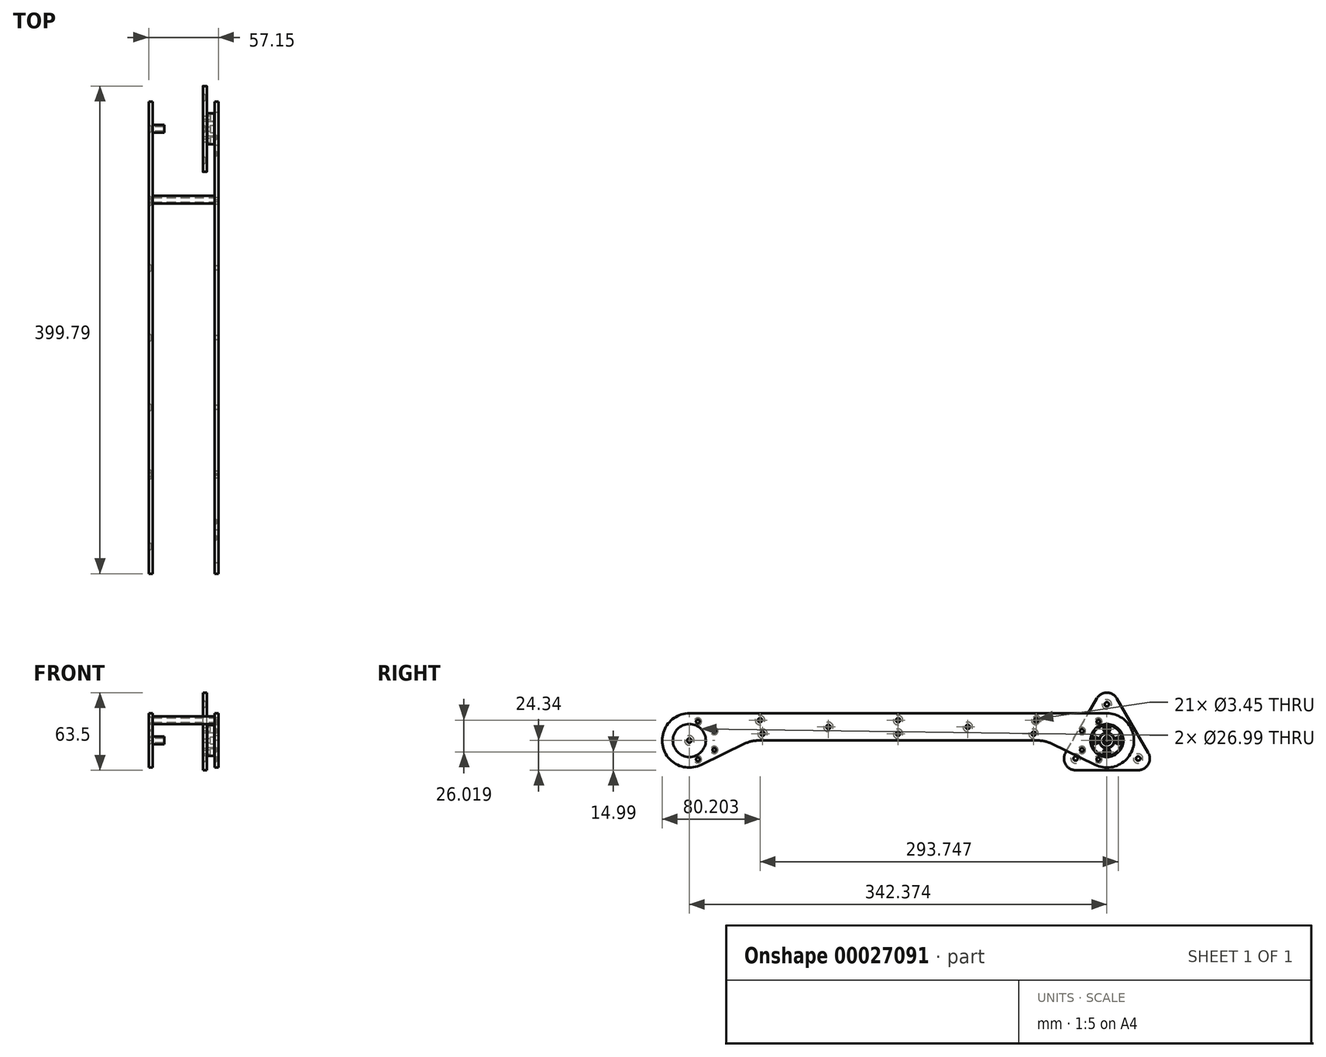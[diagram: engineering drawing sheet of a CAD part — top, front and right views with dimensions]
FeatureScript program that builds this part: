
annotation { "Feature Type Name" : "Feature", "Feature Type Description" : "" }
export const myFeature = defineFeature(function(context is Context, id is Id, definition is map)
    precondition{}
    {
        {
            var Q0;
            Q0=qCreatedBy(makeId("Right.planeOp"),FACE);
            var sketch = newSketch(context, id + "F0", { "sketchPlane" : qUnion([Q0])});
            skCircle(sketch, "E0.cCircle", {"center": v(0, 0) * mm, "radius": 29.63 * mm, "construction": true});
            skLineSegment(sketch, "E0.0", {"start": v(25.66, -14.82) * mm, "end": v(-25.66, -14.82) * mm, "construction": true});
            skLineSegment(sketch, "E0.1", {"start": v(-25.66, -14.82) * mm, "end": v(0, 29.63) * mm, "construction": true});
            skLineSegment(sketch, "E0.2", {"start": v(0, 29.63) * mm, "end": v(25.66, -14.82) * mm, "construction": true});
            skCircle(sketch, "E1", {"center": v(25.66, -14.82) * mm, "radius": 25.4 * mm});
            skCircle(sketch, "E2", {"center": v(-25.66, -14.82) * mm, "radius": 25.4 * mm});
            skCircle(sketch, "E3", {"center": v(0, 29.63) * mm, "radius": 25.4 * mm});
            skCircle(sketch, "E4", {"center": v(0, 29.63) * mm, "radius": 14.82 * mm, "construction": true});
            skCircle(sketch, "E5", {"center": v(25.66, -14.82) * mm, "radius": 14.82 * mm, "construction": true});
            skCircle(sketch, "E6", {"center": v(-25.66, -14.82) * mm, "radius": 14.82 * mm, "construction": true});
            skCircle(sketch, "E7", {"center": v(0, 0) * mm, "radius": 14.82 * mm, "construction": true});
            skCircle(sketch, "E8", {"center": v(0, 0) * mm, "radius": 55.03 * mm, "construction": true});
            skCircle(sketch, "E9", {"center": v(0, 0) * mm, "radius": 12.7 * mm});
            skCircle(sketch, "E10", {"center": v(0, 0) * mm, "radius": 3 * mm});
            skCircle(sketch, "E11.cCircle", {"center": v(0, 29.63) * mm, "radius": 8 * mm, "construction": true});
            skLineSegment(sketch, "E11.0", {"start": v(-5.66, 23.98) * mm, "end": v(-5.66, 35.3) * mm});
            skLineSegment(sketch, "E11.1", {"start": v(-5.66, 35.3) * mm, "end": v(5.66, 35.3) * mm});
            skLineSegment(sketch, "E11.2", {"start": v(5.66, 35.3) * mm, "end": v(5.66, 23.98) * mm});
            skLineSegment(sketch, "E11.3", {"start": v(5.66, 23.98) * mm, "end": v(-5.66, 23.98) * mm});
            skCircle(sketch, "E12", {"center": v(5.66, 35.3) * mm, "radius": 2.87 * mm});
            skCircle(sketch, "E13", {"center": v(0, 0) * mm, "radius": 4.23 * mm, "construction": true});
            skSolve(sketch);
        }
        {
            var Q0;
            Q0=qCreatedBy(makeId("Right.planeOp"),FACE);
            var sketch = newSketch(context, id + "F1", { "sketchPlane" : qUnion([Q0])});
            skPoint(sketch, "E14.0", {"position": v(0, 29.63) * mm});
            skPoint(sketch, "E14.1", {"position": v(-25.66, -14.82) * mm});
            skPoint(sketch, "E14.2", {"position": v(25.66, -14.82) * mm});
            skArc(sketch, "E15", {"start": v(8.25, 34.4) * mm, "mid": v(0, 39.16) * mm, "end": v(-8.25, 34.4) * mm});
            skArc(sketch, "E16", {"start": v(-33.91, -10.05) * mm, "mid": v(-33.91, -19.58) * mm, "end": v(-25.66, -24.34) * mm});
            skArc(sketch, "E17", {"start": v(25.66, -24.34) * mm, "mid": v(33.91, -19.58) * mm, "end": v(33.91, -10.05) * mm});
            skLineSegment(sketch, "E18", {"start": v(8.25, 34.4) * mm, "end": v(33.91, -10.05) * mm});
            skLineSegment(sketch, "E19", {"start": v(25.66, -24.34) * mm, "end": v(-25.66, -24.34) * mm});
            skLineSegment(sketch, "E20", {"start": v(-33.91, -10.05) * mm, "end": v(-8.25, 34.4) * mm});
            skCircle(sketch, "E21", {"center": v(0, 29.63) * mm, "radius": 1.78 * mm});
            skCircle(sketch, "E22", {"center": v(-25.66, -14.82) * mm, "radius": 1.78 * mm});
            skCircle(sketch, "E23", {"center": v(25.66, -14.82) * mm, "radius": 1.78 * mm});
            skSolve(sketch);
        }
        {
            var Q0;
            Q0 = qSketchRegion(id + "F1", true);
            extrude(context, id + "F2", {"entities" : qUnion([Q0]), "depth" : 3.17 * mm});
        }
        {
            var Q0;
            Q0=makeQuery(id+"F2.opExtrude","CAP_FACE",FACE,{"disambiguationData":[OSD([sQuery(id+"F1.wireOp",EDGE,"E15"),sQuery(id+"F1.wireOp",EDGE,"E16"),sQuery(id+"F1.wireOp",EDGE,"E17"),sQuery(id+"F1.wireOp",EDGE,"E18"),sQuery(id+"F1.wireOp",EDGE,"E19"),sQuery(id+"F1.wireOp",EDGE,"E20"),sQuery(id+"F1.wireOp",EDGE,"E21"),sQuery(id+"F1.wireOp",EDGE,"E22"),sQuery(id+"F1.wireOp",EDGE,"E23")])],"isStart":false});
            var sketch = newSketch(context, id + "F3", { "sketchPlane" : qUnion([Q0])});
            skCircle(sketch, "E24", {"center": v(0, 0) * mm, "radius": 12.7 * mm});
            skCircle(sketch, "E25", {"center": v(0, 0) * mm, "radius": 6 * mm});
            skCircle(sketch, "E26.cCircle", {"center": v(0, 0) * mm, "radius": 9.35 * mm, "construction": true});
            skLineSegment(sketch, "E26.0", {"start": v(0, 9.35) * mm, "end": v(9.35, 0) * mm, "construction": true});
            skLineSegment(sketch, "E26.1", {"start": v(9.35, 0) * mm, "end": v(0, -9.35) * mm, "construction": true});
            skLineSegment(sketch, "E26.2", {"start": v(0, -9.35) * mm, "end": v(-9.35, 0) * mm, "construction": true});
            skLineSegment(sketch, "E26.3", {"start": v(-9.35, 0) * mm, "end": v(0, 9.35) * mm, "construction": true});
            skCircle(sketch, "E27", {"center": v(0, 9.35) * mm, "radius": 2.87 * mm, "construction": true});
            skLineSegment(sketch, "E28", {"start": v(0, 12.7) * mm, "end": v(0, 6) * mm, "construction": true});
            skCircle(sketch, "E29", {"center": v(-7, 0) * mm, "radius": 18.5 * mm, "construction": true});
            skCircle(sketch, "E30.cCircle", {"center": v(-7, 0) * mm, "radius": 15.5 * mm, "construction": true});
            skLineSegment(sketch, "E30.0", {"start": v(-7, -15.5) * mm, "end": v(-20.42, -7.75) * mm, "construction": true});
            skLineSegment(sketch, "E30.1", {"start": v(-20.42, -7.75) * mm, "end": v(-20.42, 7.75) * mm, "construction": true});
            skLineSegment(sketch, "E30.2", {"start": v(-20.42, 7.75) * mm, "end": v(-7, 15.5) * mm, "construction": true});
            skLineSegment(sketch, "E30.3", {"start": v(-7, 15.5) * mm, "end": v(6.42, 7.75) * mm, "construction": true});
            skLineSegment(sketch, "E30.4", {"start": v(6.42, 7.75) * mm, "end": v(6.42, -7.75) * mm, "construction": true});
            skLineSegment(sketch, "E30.5", {"start": v(6.42, -7.75) * mm, "end": v(-7, -15.5) * mm, "construction": true});
            skCircle(sketch, "E31", {"center": v(-7, -15.5) * mm, "radius": 3 * mm, "construction": true});
            skSolve(sketch);
        }
        {
            var Q0;
            Q0 = qSketchRegion(id + "F3", true);
            extrude(context, id + "F4", {"entities" : qUnion([Q0]), "depth" : 6.35 * mm});
        }
        {
            var Q0;
            Q0=makeQuery(id+"F4.opExtrude","CAP_FACE",FACE,{"disambiguationData":[OSD([sQuery(id+"F3.wireOp",EDGE,"E24"),sQuery(id+"F3.wireOp",EDGE,"E25")])],"isStart":false});
            var sketch = newSketch(context, id + "F5", { "sketchPlane" : qUnion([Q0])});
            skPoint(sketch, "E32.0", {"position": v(0, 9.35) * mm});
            skPoint(sketch, "E32.1", {"position": v(-9.35, 0) * mm});
            skPoint(sketch, "E32.2", {"position": v(0, -9.35) * mm});
            skPoint(sketch, "E32.3", {"position": v(9.35, 0) * mm});
            skSolve(sketch);
        }
        {
            var Q0;
            Q0=sQuery(id+"F5.wireOp",VERTEX,"E32.0");
            var Q1;
            Q1=sQuery(id+"F5.wireOp",VERTEX,"E32.1");
            var Q2;
            Q2=sQuery(id+"F5.wireOp",VERTEX,"E32.2");
            var Q3;
            Q3=sQuery(id+"F5.wireOp",VERTEX,"E32.3");
            var Q4;
            Q4=makeQuery(id+"F4.opExtrude","SWEPT_BODY",BODY,{"disambiguationData":[OSD([sQuery(id+"F3.wireOp",EDGE,"E24"),sQuery(id+"F3.wireOp",EDGE,"E25")])]});
            hole(context, id + "F6", {"style" : HoleStyle.C_BORE, "holeDiameter" : 3.45 * mm, "cBoreDiameter" : 5.74 * mm, "cBoreDepth" : 3.45 * mm, "endStyle" : HoleEndStyle.THROUGH, "locations" : qUnion([Q0, Q1, Q2, Q3]), "scope" : qUnion([Q4])});
        }
        {
            var Q0;
            Q0=makeQuery(id+"F4.opExtrude","SWEPT_FACE",FACE,{"disambiguationData":[OSD([sQuery(id+"F3.wireOp",EDGE,"E24")])]});
            var Q1;
            Q1=makeQuery(id+"F4.opExtrude","SWEPT_FACE",FACE,{"disambiguationData":[OSD([sQuery(id+"F3.wireOp",EDGE,"E25")])]});
            chamfer(context, id + "F7", {"entities" : qUnion([Q0, Q1]), "width" : 0.25 * mm, "tangentPropagation" : true});
        }
        {
            var Q0;
            Q0=sQuery(id+"F3.wireOp",VERTEX,"E26.3.end");
            var Q1;
            Q1=sQuery(id+"F3.wireOp",VERTEX,"E26.3.start");
            var Q2;
            Q2=sQuery(id+"F3.wireOp",VERTEX,"E26.2.start");
            var Q3;
            Q3=sQuery(id+"F3.wireOp",VERTEX,"E26.1.start");
            var Q4;
            Q4=makeQuery(id+"F2.opExtrude","SWEPT_BODY",BODY,{"disambiguationData":[OSD([sQuery(id+"F1.wireOp",EDGE,"E15"),sQuery(id+"F1.wireOp",EDGE,"E16"),sQuery(id+"F1.wireOp",EDGE,"E17"),sQuery(id+"F1.wireOp",EDGE,"E18"),sQuery(id+"F1.wireOp",EDGE,"E19"),sQuery(id+"F1.wireOp",EDGE,"E20"),sQuery(id+"F1.wireOp",EDGE,"E21"),sQuery(id+"F1.wireOp",EDGE,"E22"),sQuery(id+"F1.wireOp",EDGE,"E23")])]});
            hole(context, id + "F8", {"style" : HoleStyle.SIMPLE, "holeDiameter" : 2.7 * mm, "endStyle" : HoleEndStyle.THROUGH, "locations" : qUnion([Q0, Q1, Q2, Q3]), "scope" : qUnion([Q4])});
        }
        {
            var Q0;
            Q0=sQuery(id+"F3.wireOp",VERTEX,"E24.center");
            var Q1;
            Q1=makeQuery(id+"F2.opExtrude","SWEPT_BODY",BODY,{"disambiguationData":[OSD([sQuery(id+"F1.wireOp",EDGE,"E15"),sQuery(id+"F1.wireOp",EDGE,"E16"),sQuery(id+"F1.wireOp",EDGE,"E17"),sQuery(id+"F1.wireOp",EDGE,"E18"),sQuery(id+"F1.wireOp",EDGE,"E19"),sQuery(id+"F1.wireOp",EDGE,"E20"),sQuery(id+"F1.wireOp",EDGE,"E21"),sQuery(id+"F1.wireOp",EDGE,"E22"),sQuery(id+"F1.wireOp",EDGE,"E23")])]});
            hole(context, id + "F9", {"style" : HoleStyle.SIMPLE, "holeDiameter" : 12.7 * mm, "endStyle" : HoleEndStyle.THROUGH, "locations" : qUnion([Q0]), "scope" : qUnion([Q1])});
        }
        {
            var Q0;
            Q0=makeQuery(id+"F4.opExtrude","CAP_FACE",FACE,{"disambiguationData":[OSD([sQuery(id+"F3.wireOp",EDGE,"E24"),sQuery(id+"F3.wireOp",EDGE,"E25")])],"isStart":false});
            var sketch = newSketch(context, id + "F10", { "sketchPlane" : qUnion([Q0])});
            skCircle(sketch, "E33.0", {"center": v(0, 0) * mm, "radius": 13.5 * mm});
            skPoint(sketch, "E34.0", {"position": v(-7, 15.5) * mm});
            skPoint(sketch, "E34.1", {"position": v(-20.42, 7.75) * mm});
            skPoint(sketch, "E34.2", {"position": v(-20.42, -7.75) * mm});
            skPoint(sketch, "E34.3", {"position": v(-7, -15.5) * mm});
            skCircle(sketch, "E34.4", {"center": v(-7, 0) * mm, "radius": 18.5 * mm, "construction": true});
            skArc(sketch, "E35", {"start": v(-9.72, -19.99) * mm, "mid": v(21.66, -4.99) * mm, "end": v(0, 22.22) * mm});
            skLineSegment(sketch, "E36", {"start": v(-399.79, -40.22) * mm, "end": v(57.41, -40.22) * mm, "construction": true});
            skLineSegment(sketch, "E37", {"start": v(57.41, -40.22) * mm, "end": v(57.41, 416.98) * mm, "construction": true});
            skLineSegment(sketch, "E38", {"start": v(57.41, 416.98) * mm, "end": v(-399.79, 416.98) * mm, "construction": true});
            skLineSegment(sketch, "E39", {"start": v(-399.79, 416.98) * mm, "end": v(-399.79, -40.22) * mm, "construction": true});
            skLineSegment(sketch, "E40", {"start": v(-171.19, 416.98) * mm, "end": v(-171.19, -40.22) * mm, "construction": true});
            skCircle(sketch, "E41.MirrorC", {"center": v(-342.37, 0) * mm, "radius": 13.5 * mm});
            skPoint(sketch, "E42.MirrorP", {"position": v(-335.37, -15.5) * mm});
            skPoint(sketch, "E43.MirrorP", {"position": v(-321.95, -7.75) * mm});
            skPoint(sketch, "E44.MirrorP", {"position": v(-321.95, 7.75) * mm});
            skPoint(sketch, "E45.MirrorP", {"position": v(-335.37, 15.5) * mm});
            skArc(sketch, "E46.MirrorC", {"start": v(-332.65, -19.99) * mm, "mid": v(-364.03, -4.99) * mm, "end": v(-342.37, 22.22) * mm});
            skLineSegment(sketch, "E47", {"start": v(-342.37, 22.22) * mm, "end": v(0, 22.23) * mm});
            skLineSegment(sketch, "E48", {"start": v(-9.72, -19.99) * mm, "end": v(-50.8, 0) * mm});
            skLineSegment(sketch, "E49", {"start": v(-50.8, 0) * mm, "end": v(-291.57, 0) * mm});
            skLineSegment(sketch, "E50", {"start": v(-291.57, 0) * mm, "end": v(-332.65, -19.99) * mm});
            skCircle(sketch, "E51", {"center": v(-7, -15.5) * mm, "radius": 3 * mm, "construction": true});
            skSolve(sketch);
        }
        {
            var Q0;
            Q0 = qSketchRegion(id + "F10", true);
            extrude(context, id + "F11", {"entities" : qUnion([Q0]), "depth" : 3.17 * mm});
        }
        {
            var Q0;
            Q0=makeQuery(id+"F11.opExtrude","SWEPT_EDGE",EDGE,{"disambiguationData":[OSD([sQuery(id+"F10.wireOp",EDGE,"E48"),sQuery(id+"F10.wireOp",EDGE,"E49")])]});
            var Q1;
            Q1=makeQuery(id+"F11.opExtrude","SWEPT_EDGE",EDGE,{"disambiguationData":[OSD([sQuery(id+"F10.wireOp",EDGE,"E49"),sQuery(id+"F10.wireOp",EDGE,"E50")])]});
            fillet(context, id + "F12", {"entities" : qUnion([Q0, Q1]), "radius" : 25.4 * mm, "tangentPropagation" : true, "allowEdgeOverflow" : false});
        }
        {
            var Q0;
            Q0=sQuery(id+"F10.wireOp",VERTEX,"E34.3");
            var Q1;
            Q1=sQuery(id+"F10.wireOp",VERTEX,"E34.2");
            var Q2;
            Q2=sQuery(id+"F10.wireOp",VERTEX,"E34.1");
            var Q3;
            Q3=sQuery(id+"F10.wireOp",VERTEX,"E34.0");
            var Q4;
            Q4=sQuery(id+"F10.wireOp",VERTEX,"E45.MirrorP");
            var Q5;
            Q5=sQuery(id+"F10.wireOp",VERTEX,"E44.MirrorP");
            var Q6;
            Q6=sQuery(id+"F10.wireOp",VERTEX,"E43.MirrorP");
            var Q7;
            Q7=sQuery(id+"F10.wireOp",VERTEX,"E42.MirrorP");
            var Q8;
            Q8=makeQuery(id+"F11.opExtrude","SWEPT_BODY",BODY,{"disambiguationData":[OSD([sQuery(id+"F10.wireOp",EDGE,"E33.0"),sQuery(id+"F10.wireOp",EDGE,"E35")])]});
            hole(context, id + "F13", {"style" : HoleStyle.C_SINK, "holeDiameter" : 3 * mm, "cSinkDiameter" : 6 * mm, "endStyle" : HoleEndStyle.THROUGH, "oppositeDirection" : true, "locations" : qUnion([Q0, Q1, Q2, Q3, Q4, Q5, Q6, Q7]), "scope" : qUnion([Q8]), "cSinkAngle" : 90 * degree});
        }
        {
            var Q0;
            Q0=makeQuery(id+"F11.opExtrude","CAP_FACE",FACE,{"disambiguationData":[OSD([sQuery(id+"F10.wireOp",EDGE,"E33.0"),sQuery(id+"F10.wireOp",EDGE,"E35"),sQuery(id+"F10.wireOp",EDGE,"E41.MirrorC"),sQuery(id+"F10.wireOp",EDGE,"E46.MirrorC"),sQuery(id+"F10.wireOp",EDGE,"E47"),sQuery(id+"F10.wireOp",EDGE,"E48"),sQuery(id+"F10.wireOp",EDGE,"E49"),sQuery(id+"F10.wireOp",EDGE,"E50")])],"isStart":true});
            cPlane(context, id + "F14", {"entities" : qUnion([Q0]), "cplaneType" : CPlaneType.OFFSET, "offset" : 50.8 * mm, "width" : 152.4 * mm, "height" : 152.4 * mm});
        }
        {
            var Q0;
            Q0=qCreatedBy(id+"F14.planeOp",FACE);
            var sketch = newSketch(context, id + "F15", { "sketchPlane" : qUnion([Q0])});
            skCircle(sketch, "E52", {"center": v(0, 0) * mm, "radius": 1.78 * mm});
            skCircle(sketch, "E53", {"center": v(342.37, 0) * mm, "radius": 1.78 * mm});
            skLineSegment(sketch, "E54.0.0", {"start": v(9.72, -19.99) * mm, "end": v(45.54, -2.56) * mm});
            skArc(sketch, "E54.0.1", {"start": v(45.54, -2.56) * mm, "mid": v(50.95, -0.65) * mm, "end": v(56.65, 0) * mm});
            skLineSegment(sketch, "E54.0.2", {"start": v(56.65, 0) * mm, "end": v(285.72, 0) * mm});
            skArc(sketch, "E54.0.3", {"start": v(285.72, 0) * mm, "mid": v(291.42, -0.65) * mm, "end": v(296.83, -2.56) * mm});
            skLineSegment(sketch, "E54.0.4", {"start": v(296.83, -2.56) * mm, "end": v(332.65, -19.99) * mm});
            skArc(sketch, "E54.0.5", {"start": v(332.65, -19.99) * mm, "mid": v(364.03, -4.99) * mm, "end": v(342.37, 22.22) * mm});
            skLineSegment(sketch, "E54.0.6", {"start": v(342.37, 22.22) * mm, "end": v(0, 22.23) * mm});
            skArc(sketch, "E54.0.7", {"start": v(0, 22.23) * mm, "mid": v(-21.66, -4.99) * mm, "end": v(9.72, -19.99) * mm});
            skSolve(sketch);
        }
        {
            var Q0;
            Q0 = qSketchRegion(id + "F15", true);
            extrude(context, id + "F16", {"entities" : qUnion([Q0]), "depth" : 3.17 * mm});
        }
        {
            var Q0;
            Q0=makeQuery(id+"F16.opExtrude","CAP_FACE",FACE,{"disambiguationData":[OSD([sQuery(id+"F15.wireOp",EDGE,"e8c20939-d516-41e8-ae06-daf4ae15fd7b.0.0"),sQuery(id+"F15.wireOp",EDGE,"e8c20939-d516-41e8-ae06-daf4ae15fd7b.0.1"),sQuery(id+"F15.wireOp",EDGE,"e8c20939-d516-41e8-ae06-daf4ae15fd7b.0.2"),sQuery(id+"F15.wireOp",EDGE,"e8c20939-d516-41e8-ae06-daf4ae15fd7b.0.3"),sQuery(id+"F15.wireOp",EDGE,"e8c20939-d516-41e8-ae06-daf4ae15fd7b.0.4"),sQuery(id+"F15.wireOp",EDGE,"e8c20939-d516-41e8-ae06-daf4ae15fd7b.0.5"),sQuery(id+"F15.wireOp",EDGE,"E52"),sQuery(id+"F15.wireOp",EDGE,"E53")])],"isStart":false});
            var sketch = newSketch(context, id + "F17", { "sketchPlane" : qUnion([Q0])});
            skLineSegment(sketch, "E55", {"start": v(171.19, 22.22) * mm, "end": v(171.19, 0) * mm, "construction": true});
            skCircle(sketch, "E56", {"center": v(57.98, 16.67) * mm, "radius": 4.56 * mm, "construction": true});
            skCircle(sketch, "E57", {"center": v(60.07, 5.56) * mm, "radius": 4.56 * mm, "construction": true});
            skCircle(sketch, "E58", {"center": v(0, 0) * mm, "radius": 60.33 * mm, "construction": true});
            skCircle(sketch, "E59", {"center": v(57.98, 16.67) * mm, "radius": 3.18 * mm, "construction": true});
            skPoint(sketch, "E60", {"position": v(284.4, 16.67) * mm});
            skPoint(sketch, "E61", {"position": v(282.3, 5.56) * mm});
            skPoint(sketch, "E62", {"position": v(171.19, 16.67) * mm});
            skPoint(sketch, "E63", {"position": v(171.19, 5.56) * mm});
            skPoint(sketch, "E64", {"position": v(114.04, 11.11) * mm});
            skPoint(sketch, "E65", {"position": v(228.34, 11.11) * mm});
            skPoint(sketch, "E66", {"position": v(171.19, 11.11) * mm});
            skCircle(sketch, "E67.0", {"center": v(342.37, 0) * mm, "radius": 1.78 * mm});
            skSolve(sketch);
        }
        {
            var Q0;
            Q0=sQuery(id+"F17.wireOp",VERTEX,"E59.center");
            var Q1;
            Q1=sQuery(id+"F17.wireOp",VERTEX,"E57.center");
            var Q2;
            Q2=sQuery(id+"F17.wireOp",VERTEX,"E60");
            var Q3;
            Q3=sQuery(id+"F17.wireOp",VERTEX,"E61");
            var Q4;
            Q4=sQuery(id+"F17.wireOp",VERTEX,"E65");
            var Q5;
            Q5=sQuery(id+"F17.wireOp",VERTEX,"E64");
            var Q6;
            Q6=sQuery(id+"F17.wireOp",VERTEX,"E62");
            var Q7;
            Q7=sQuery(id+"F17.wireOp",VERTEX,"E63");
            var Q8;
            Q8=sQuery(id+"F17.wireOp",VERTEX,"E58.center");
            var Q9;
            Q9=sQuery(id+"F17.wireOp",VERTEX,"E67.0.center");
            var Q10;
            Q10=makeQuery(id+"F16.opExtrude","SWEPT_BODY",BODY,{"disambiguationData":[OSD([sQuery(id+"F15.wireOp",EDGE,"e8c20939-d516-41e8-ae06-daf4ae15fd7b.0.0"),sQuery(id+"F15.wireOp",EDGE,"e8c20939-d516-41e8-ae06-daf4ae15fd7b.0.1"),sQuery(id+"F15.wireOp",EDGE,"e8c20939-d516-41e8-ae06-daf4ae15fd7b.0.2"),sQuery(id+"F15.wireOp",EDGE,"e8c20939-d516-41e8-ae06-daf4ae15fd7b.0.3"),sQuery(id+"F15.wireOp",EDGE,"e8c20939-d516-41e8-ae06-daf4ae15fd7b.0.4"),sQuery(id+"F15.wireOp",EDGE,"e8c20939-d516-41e8-ae06-daf4ae15fd7b.0.5"),sQuery(id+"F15.wireOp",EDGE,"E52"),sQuery(id+"F15.wireOp",EDGE,"E53")])]});
            var Q11;
            Q11=makeQuery(id+"F11.opExtrude","SWEPT_BODY",BODY,{"disambiguationData":[OSD([sQuery(id+"F10.wireOp",EDGE,"E33.0"),sQuery(id+"F10.wireOp",EDGE,"E35"),sQuery(id+"F10.wireOp",EDGE,"E41.MirrorC"),sQuery(id+"F10.wireOp",EDGE,"E46.MirrorC"),sQuery(id+"F10.wireOp",EDGE,"E47"),sQuery(id+"F10.wireOp",EDGE,"E48"),sQuery(id+"F10.wireOp",EDGE,"E49"),sQuery(id+"F10.wireOp",EDGE,"E50")])]});
            hole(context, id + "F18", {"style" : HoleStyle.C_SINK, "holeDiameter" : 3.45 * mm, "cSinkDiameter" : 7.8 * mm, "endStyle" : HoleEndStyle.THROUGH, "locations" : qUnion([Q0, Q1, Q2, Q3, Q4, Q5, Q6, Q7, Q8, Q9]), "scope" : qUnion([Q10, Q11]), "cSinkAngle" : 90 * degree});
        }
        {
            var Q0;
            Q0=makeQuery(id+"F11.opExtrude","CAP_FACE",FACE,{"disambiguationData":[OSD([sQuery(id+"F10.wireOp",EDGE,"E33.0"),sQuery(id+"F10.wireOp",EDGE,"E35"),sQuery(id+"F10.wireOp",EDGE,"E41.MirrorC"),sQuery(id+"F10.wireOp",EDGE,"E46.MirrorC"),sQuery(id+"F10.wireOp",EDGE,"E47"),sQuery(id+"F10.wireOp",EDGE,"E48"),sQuery(id+"F10.wireOp",EDGE,"E49"),sQuery(id+"F10.wireOp",EDGE,"E50")])],"isStart":true});
            var sketch = newSketch(context, id + "F19", { "sketchPlane" : qUnion([Q0])});
            skCircle(sketch, "E68.0", {"center": v(57.98, 16.67) * mm, "radius": 1.73 * mm});
            skCircle(sketch, "E69", {"center": v(57.98, 16.67) * mm, "radius": 3.17 * mm});
            skSolve(sketch);
        }
        {
            var Q0;
            Q0 = qSketchRegion(id + "F19", true);
            var Q1;
            Q1=makeQuery(id+"F16.opExtrude","SWEPT_BODY",BODY,{"disambiguationData":[OSD([sQuery(id+"F15.wireOp",EDGE,"e8c20939-d516-41e8-ae06-daf4ae15fd7b.0.0"),sQuery(id+"F15.wireOp",EDGE,"e8c20939-d516-41e8-ae06-daf4ae15fd7b.0.1"),sQuery(id+"F15.wireOp",EDGE,"e8c20939-d516-41e8-ae06-daf4ae15fd7b.0.2"),sQuery(id+"F15.wireOp",EDGE,"e8c20939-d516-41e8-ae06-daf4ae15fd7b.0.3"),sQuery(id+"F15.wireOp",EDGE,"e8c20939-d516-41e8-ae06-daf4ae15fd7b.0.4"),sQuery(id+"F15.wireOp",EDGE,"e8c20939-d516-41e8-ae06-daf4ae15fd7b.0.5"),sQuery(id+"F15.wireOp",EDGE,"E52"),sQuery(id+"F15.wireOp",EDGE,"E53")])]});
            extrude(context, id + "F20", {"entities" : qUnion([Q0]), "endBound" : BoundingType.UP_TO_BODY, "endBoundEntityBody" : qUnion([Q1]), "depth" : 25.4 * mm});
        }
        {
            var Q0;
            Q0=makeQuery(id+"F16.opExtrude","CAP_FACE",FACE,{"disambiguationData":[OSD([sQuery(id+"F15.wireOp",EDGE,"e8c20939-d516-41e8-ae06-daf4ae15fd7b.0.0"),sQuery(id+"F15.wireOp",EDGE,"e8c20939-d516-41e8-ae06-daf4ae15fd7b.0.1"),sQuery(id+"F15.wireOp",EDGE,"e8c20939-d516-41e8-ae06-daf4ae15fd7b.0.2"),sQuery(id+"F15.wireOp",EDGE,"e8c20939-d516-41e8-ae06-daf4ae15fd7b.0.3"),sQuery(id+"F15.wireOp",EDGE,"e8c20939-d516-41e8-ae06-daf4ae15fd7b.0.4"),sQuery(id+"F15.wireOp",EDGE,"e8c20939-d516-41e8-ae06-daf4ae15fd7b.0.5"),sQuery(id+"F15.wireOp",EDGE,"E52"),sQuery(id+"F15.wireOp",EDGE,"E53")])],"isStart":true});
            var sketch = newSketch(context, id + "F21", { "sketchPlane" : qUnion([Q0])});
            skCircle(sketch, "E70.0", {"center": v(0, 0) * mm, "radius": 1.78 * mm});
            skCircle(sketch, "E71", {"center": v(0, 0) * mm, "radius": 3.18 * mm});
            skCircle(sketch, "E72", {"center": v(0, 0) * mm, "radius": 4.76 * mm});
            skSolve(sketch);
        }
        {
            var Q0;
            Q0=makeQuery(id+"F21.imprint","IMPRINT",FACE,{"disambiguationData":[TD([[makeQuery(id+"F21.imprint","IMPRINT",EDGE,{"derivedFrom":sQuery(id+"F21.wireOp",EDGE,"E70.0")}),1.0]])]});
            extrude(context, id + "F22", {"entities" : qUnion([Q0]), "depth" : 9.52 * mm});
        }
        {
            var Q0;
            Q0=sQuery(id+"F1.wireOp",VERTEX,"E14.0");
            var Q1;
            Q1=sQuery(id+"F1.wireOp",VERTEX,"E14.2");
            var Q2;
            Q2=sQuery(id+"F1.wireOp",VERTEX,"E14.1");
            var Q3;
            Q3=makeQuery(id+"F2.opExtrude","SWEPT_BODY",BODY,{"disambiguationData":[OSD([sQuery(id+"F1.wireOp",EDGE,"E15"),sQuery(id+"F1.wireOp",EDGE,"E16"),sQuery(id+"F1.wireOp",EDGE,"E17"),sQuery(id+"F1.wireOp",EDGE,"E18"),sQuery(id+"F1.wireOp",EDGE,"E19"),sQuery(id+"F1.wireOp",EDGE,"E20"),sQuery(id+"F1.wireOp",EDGE,"E21"),sQuery(id+"F1.wireOp",EDGE,"E22"),sQuery(id+"F1.wireOp",EDGE,"E23")])]});
            hole(context, id + "F23", {"style" : HoleStyle.C_SINK, "holeDiameter" : 3.45 * mm, "cSinkDiameter" : 7.8 * mm, "endStyle" : HoleEndStyle.THROUGH, "oppositeDirection" : true, "locations" : qUnion([Q0, Q1, Q2]), "scope" : qUnion([Q3]), "cSinkAngle" : 90 * degree});
        }
    });
